# Revit family: en-halla-lumia-accessories-suspendedrfa
name_source: partatom
category: Специальное оборудование
revit_build: Autodesk Revit 2017 (Build: 20160225_1515(x64)
units: mm (PartAtom-declared; Revit-internal decimal feet)

## family parameters
Заголовок OmniClass = General Luminaries, Non Directional
Номер OmniClass = 23.80.70.11.11
Общий = Нет
Основа = Грань
При загрузке вырезать с полостями = Нет
Размер круглого соединителя = Использовать диаметр
Тип детали = Нормальный
Точка расчета площади = Нет

## types (5) — shared parameters
Colour of luminaire = Aluminium - anodised
Lighting height = 36 мм
Lighting length = 1000 мм
Lighting width = 230 мм
Material of luminaire = Aluminium
URL = http://www.halla.cz
Výška zavěšení maximální = 2000 мм
Изготовитель = HALLA
Код по классификатору = D5020230
Отметка по умолчанию = 1000 мм

## per-type parameters (varying)
| type | L | QR code | T | Tubus | X |
| 10-0001, E - profile for modules | Нет |  | Нет | Да | Нет |
| 10-0011, E - body profile | Нет | http://file-system.ru | Нет | Да | Нет |
| 10-0003, E - joint L | Да |  | Нет | Нет | Нет |
| 10-0004, E - joint T | Нет |  | Да | Нет | Нет |
| 10-0005, E - joint X | Нет |  | Нет | Нет | Да |
